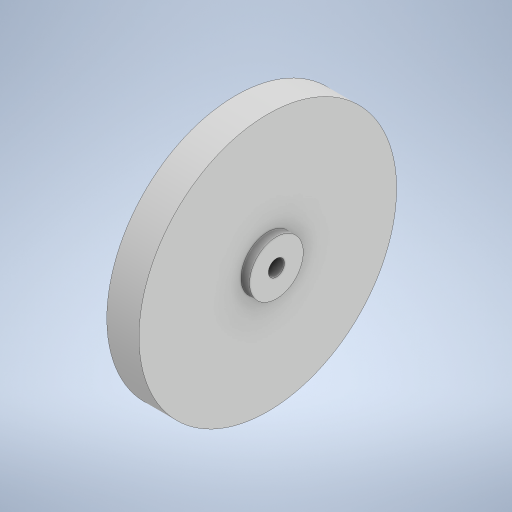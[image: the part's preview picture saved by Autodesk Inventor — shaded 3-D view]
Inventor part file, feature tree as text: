
AUTODESK INVENTOR PART (.ipt)
format: ipt  version: 2024 (Build 280153000, 153)  size: 227,328 bytes
history: native  units: mm
features: extrude x4, sketch x4, other x1
ambient origin geometry x8: Origin, YZ Plane, XZ Plane, XY Plane, X Axis, Y Axis, Z Axis, Center Point
bodies: Body1 (feature_tree)
feature tree (9):
  other  "wheel"
  extrude  "Extrusion1"  Depth=50.0mm
  extrude  "Extrusion2"  Depth=30.0mm TaperAngle=0.0deg
  extrude  "Extrusion3"  Depth=20.0mm
  extrude  "Extrusion4"  Depth=8.0mm
  sketch  "Sketch1"  dims[d0=240.0mm d1=50.0mm]
  sketch  "Sketch2"  dims[d2=15.0mm d3=30.0mm d4=0.0mm]
  sketch  "Sketch3"  dims[d5=20.0mm d6=0.0mm d7=15.0mm]
  sketch  "Sketch4"  dims[d8=20.0mm d9=0.0mm d10=50.0mm d11=8.0mm d12=0.0mm]
